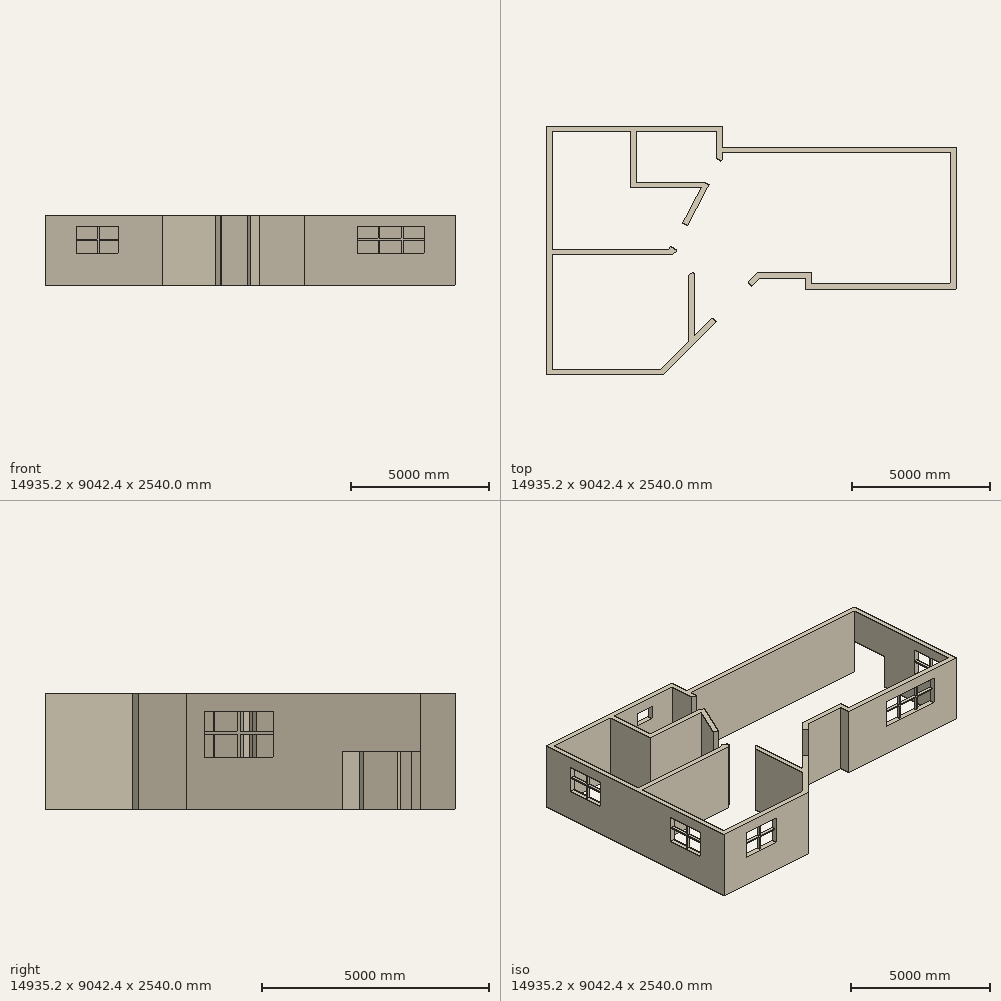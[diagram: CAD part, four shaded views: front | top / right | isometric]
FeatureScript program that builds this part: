
annotation { "Feature Type Name" : "Feature", "Feature Type Description" : "" }
export const myFeature = defineFeature(function(context is Context, id is Id, definition is map)
    precondition{}
    {
        {
            var Q0;
            Q0=qCreatedBy(makeId("Top.planeOp"),FACE);
            var sketch = newSketch(context, id + "F0", { "sketchPlane" : qUnion([Q0])});
            skLineSegment(sketch, "E0.bottom", {"start": v(0, 0) * mm, "end": v(14935.2, 0) * mm});
            skLineSegment(sketch, "E0.top", {"start": v(0, 10668) * mm, "end": v(14935.2, 10668) * mm});
            skLineSegment(sketch, "E0.left", {"start": v(0, 0) * mm, "end": v(0, 10668) * mm});
            skLineSegment(sketch, "E0.right", {"start": v(14935.2, 0) * mm, "end": v(14935.2, 10668) * mm});
            skLineSegment(sketch, "E1", {"start": v(6400.8, 10668) * mm, "end": v(6400.8, 9906) * mm});
            skLineSegment(sketch, "E2", {"start": v(6400.8, 9906) * mm, "end": v(14935.2, 9906) * mm});
            skLineSegment(sketch, "E3", {"start": v(0, 1625.6) * mm, "end": v(4279.65, 1625.6) * mm});
            skLineSegment(sketch, "E4", {"start": v(203.2, 1828.8) * mm, "end": v(2071.3, 1828.8) * mm});
            skLineSegment(sketch, "E5", {"start": v(203.2, 1828.8) * mm, "end": v(203.2, 5994.4) * mm});
            skLineSegment(sketch, "E6", {"start": v(203.2, 10464.8) * mm, "end": v(3073.4, 10464.8) * mm});
            skLineSegment(sketch, "E7", {"start": v(6197.6, 10464.8) * mm, "end": v(6197.6, 9702.8) * mm});
            skLineSegment(sketch, "E8", {"start": v(6400.8, 9702.8) * mm, "end": v(14732, 9702.8) * mm});
            skLineSegment(sketch, "E9", {"start": v(3073.4, 10464.8) * mm, "end": v(3073.4, 8432.8) * mm});
            skLineSegment(sketch, "E10", {"start": v(3073.4, 8432.8) * mm, "end": v(5640.45, 8432.8) * mm});
            skLineSegment(sketch, "E11", {"start": v(3276.6, 8636) * mm, "end": v(5746.81, 8636) * mm});
            skLineSegment(sketch, "E12", {"start": v(3276.6, 8636) * mm, "end": v(3276.6, 10464.8) * mm});
            skLineSegment(sketch, "E13", {"start": v(203.2, 6197.6) * mm, "end": v(4470.4, 6197.6) * mm});
            skLineSegment(sketch, "E14", {"start": v(203.2, 5994.4) * mm, "end": v(4592.55, 5994.4) * mm});
            skLineSegment(sketch, "E15", {"start": v(6400.8, 9702.8) * mm, "end": v(6400.8, 9448.8) * mm});
            skLineSegment(sketch, "E16", {"start": v(6197.6, 9497.16) * mm, "end": v(6197.6, 9702.8) * mm});
            skLineSegment(sketch, "E17", {"start": v(6197.6, 9497.16) * mm, "end": v(6194.44, 9491.13) * mm});
            skLineSegment(sketch, "E18", {"start": v(5143.93, 7047.74) * mm, "end": v(5926.18, 8542.1) * mm});
            skLineSegment(sketch, "E19.trimOffspring", {"start": v(5640.45, 8432.8) * mm, "end": v(4964.57, 7141.63) * mm});
            skLineSegment(sketch, "E20.trimOffspring", {"start": v(203.2, 6197.6) * mm, "end": v(203.2, 10464.8) * mm});
            skLineSegment(sketch, "E21", {"start": v(9448.8, 4724.4) * mm, "end": v(14935.2, 4724.4) * mm});
            skLineSegment(sketch, "E22", {"start": v(9652, 4927.6) * mm, "end": v(14732, 4927.6) * mm});
            skPoint(sketch, "E23.orphan", {"position": v(9448.8, 3711.85) * mm});
            skPoint(sketch, "E24.orphan", {"position": v(14935.2, 3711.85) * mm});
            skLineSegment(sketch, "E25", {"start": v(14732, 9702.8) * mm, "end": v(14732, 4927.6) * mm});
            skPoint(sketch, "E26.trimOffspring.end.orphan", {"position": v(3962.4, 3711.85) * mm});
            skLineSegment(sketch, "E27", {"start": v(9652, 4927.6) * mm, "end": v(9652, 5334) * mm});
            skLineSegment(sketch, "E28", {"start": v(9652, 5334) * mm, "end": v(7700.69, 5334) * mm});
            skLineSegment(sketch, "E29", {"start": v(7784.85, 5130.8) * mm, "end": v(9448.8, 5130.8) * mm});
            skLineSegment(sketch, "E30", {"start": v(9448.8, 5130.8) * mm, "end": v(9448.8, 4724.4) * mm});
            skPoint(sketch, "E31.orphan", {"position": v(9652, 4724.4) * mm});
            skLineSegment(sketch, "E32", {"start": v(2071.3, 1828.8) * mm, "end": v(4195.49, 1828.8) * mm});
            skLineSegment(sketch, "E33", {"start": v(4195.49, 1828.8) * mm, "end": v(5181.9, 2815.22) * mm});
            skLineSegment(sketch, "E34", {"start": v(4279.65, 1625.6) * mm, "end": v(6192, 3537.95) * mm});
            skPoint(sketch, "E35.orphan", {"position": v(4195.49, 1625.6) * mm});
            skLineSegment(sketch, "E36", {"start": v(5181.9, 5230.03) * mm, "end": v(5181.9, 2815.22) * mm});
            skLineSegment(sketch, "E37", {"start": v(4696.3, 6192.61) * mm, "end": v(4753.47, 6118.48) * mm});
            skLineSegment(sketch, "E38", {"start": v(5385.1, 5299.27) * mm, "end": v(5385.1, 3018.42) * mm});
            skLineSegment(sketch, "E39.trimOffspring", {"start": v(5385.1, 3018.42) * mm, "end": v(6048.32, 3681.63) * mm});
            skLineSegment(sketch, "E40", {"start": v(7341.48, 4974.79) * mm, "end": v(7485.16, 4831.1) * mm});
            skLineSegment(sketch, "E41", {"start": v(6048.32, 3681.63) * mm, "end": v(6192, 3537.95) * mm});
            skLineSegment(sketch, "E42.trimOffspring", {"start": v(7485.16, 4831.1) * mm, "end": v(7784.85, 5130.8) * mm});
            skLineSegment(sketch, "E43.trimOffspring", {"start": v(7341.48, 4974.79) * mm, "end": v(7700.69, 5334) * mm});
            skLineSegment(sketch, "E44", {"start": v(4592.55, 5994.4) * mm, "end": v(4753.47, 6118.48) * mm});
            skLineSegment(sketch, "E45", {"start": v(5181.9, 5230.03) * mm, "end": v(5342.83, 5354.1) * mm});
            skLineSegment(sketch, "E46.trimOffspring", {"start": v(5342.83, 5354.1) * mm, "end": v(5385.1, 5299.27) * mm});
            skLineSegment(sketch, "E47", {"start": v(4696.3, 6192.61) * mm, "end": v(4516.94, 6286.5) * mm});
            skLineSegment(sketch, "E48", {"start": v(5143.93, 7047.74) * mm, "end": v(4964.57, 7141.63) * mm});
            skLineSegment(sketch, "E49.trimOffspring", {"start": v(4516.94, 6286.5) * mm, "end": v(4470.4, 6197.6) * mm});
            skLineSegment(sketch, "E50", {"start": v(5746.81, 8636) * mm, "end": v(5926.18, 8542.1) * mm});
            skLineSegment(sketch, "E51", {"start": v(6194.44, 9491.13) * mm, "end": v(6373.8, 9397.23) * mm});
            skLineSegment(sketch, "E52.trimOffspring", {"start": v(6373.8, 9397.23) * mm, "end": v(6400.8, 9448.8) * mm});
            skPoint(sketch, "E53.orphan", {"position": v(3073.4, 10668) * mm});
            skLineSegment(sketch, "E54.trimOffspring", {"start": v(3276.6, 10464.8) * mm, "end": v(6197.6, 10464.8) * mm});
            skPoint(sketch, "E55.orphan", {"position": v(3276.6, 10668) * mm});
            skSolve(sketch);
        }
        {
            var Q0;
            {var subQ14=sQuery(id+"F0.wireOp",EDGE,"E1");Q0=makeQuery(id+"F0.imprint","IMPRINT",FACE,{"disambiguationData":[TD([[makeQuery(id+"F0.imprint","IMPRINT",EDGE,{"derivedFrom":subQ14}),-1.0]])]});}
            extrude(context, id + "F1", {"entities" : qUnion([Q0]), "depth" : 2540 * mm, "offsetDistance" : 25.4 * mm});
        }
        {
            var Q0;
            Q0=makeQuery(id+"F1.opExtrude","SWEPT_FACE",FACE,{"disambiguationData":[OSD([sQuery(id+"F0.wireOp",EDGE,"E0.left")])]});
            var sketch = newSketch(context, id + "F2", { "sketchPlane" : qUnion([Q0])});
            skLineSegment(sketch, "E56.bottom", {"start": v(-9448.8, 2159) * mm, "end": v(-7924.8, 2159) * mm});
            skLineSegment(sketch, "E56.top", {"start": v(-9448.8, 1143) * mm, "end": v(-7924.8, 1143) * mm});
            skLineSegment(sketch, "E56.left", {"start": v(-9448.8, 2159) * mm, "end": v(-9448.8, 1143) * mm});
            skLineSegment(sketch, "E56.right", {"start": v(-7924.8, 2159) * mm, "end": v(-7924.8, 1143) * mm});
            skLineSegment(sketch, "E57.bottom", {"start": v(-4368.8, 2159) * mm, "end": v(-2844.8, 2159) * mm});
            skLineSegment(sketch, "E57.top", {"start": v(-4368.8, 1143) * mm, "end": v(-2844.8, 1143) * mm});
            skLineSegment(sketch, "E57.left", {"start": v(-4368.8, 2159) * mm, "end": v(-4368.8, 1143) * mm});
            skLineSegment(sketch, "E57.right", {"start": v(-2844.8, 2159) * mm, "end": v(-2844.8, 1143) * mm});
            skLineSegment(sketch, "E58.bottom", {"start": v(-8712.2, 2159) * mm, "end": v(-8661.4, 2159) * mm});
            skLineSegment(sketch, "E58.top", {"start": v(-8712.2, 1143) * mm, "end": v(-8661.4, 1143) * mm});
            skLineSegment(sketch, "E58.left", {"start": v(-8712.2, 2159) * mm, "end": v(-8712.2, 1701.8) * mm});
            skLineSegment(sketch, "E58.right", {"start": v(-8661.4, 2159) * mm, "end": v(-8661.4, 1701.8) * mm});
            skLineSegment(sketch, "E59.bottom", {"start": v(-9448.8, 1701.8) * mm, "end": v(-8712.2, 1701.8) * mm});
            skLineSegment(sketch, "E59.top", {"start": v(-9448.8, 1651) * mm, "end": v(-8712.2, 1651) * mm});
            skLineSegment(sketch, "E59.left", {"start": v(-9448.8, 1701.8) * mm, "end": v(-9448.8, 1651) * mm});
            skLineSegment(sketch, "E59.right", {"start": v(-7924.8, 1701.8) * mm, "end": v(-7924.8, 1651) * mm});
            skLineSegment(sketch, "E60.bottom", {"start": v(-4368.8, 1701.8) * mm, "end": v(-3632.2, 1701.8) * mm});
            skLineSegment(sketch, "E60.top", {"start": v(-4368.8, 1651) * mm, "end": v(-3632.2, 1651) * mm});
            skLineSegment(sketch, "E60.left", {"start": v(-4368.8, 1701.8) * mm, "end": v(-4368.8, 1651) * mm});
            skLineSegment(sketch, "E60.right", {"start": v(-2844.8, 1701.8) * mm, "end": v(-2844.8, 1651) * mm});
            skLineSegment(sketch, "E61.bottom", {"start": v(-3632.2, 2159) * mm, "end": v(-3581.4, 2159) * mm});
            skLineSegment(sketch, "E61.top", {"start": v(-3632.2, 1143) * mm, "end": v(-3581.4, 1143) * mm});
            skLineSegment(sketch, "E61.left", {"start": v(-3632.2, 2159) * mm, "end": v(-3632.2, 1701.8) * mm});
            skLineSegment(sketch, "E61.right", {"start": v(-3581.4, 2159) * mm, "end": v(-3581.4, 1701.8) * mm});
            skLineSegment(sketch, "E62.trimOffspring", {"start": v(-8661.4, 1701.8) * mm, "end": v(-7924.8, 1701.8) * mm});
            skLineSegment(sketch, "E63.trimOffspring", {"start": v(-8712.2, 1651) * mm, "end": v(-8712.2, 1143) * mm});
            skLineSegment(sketch, "E64.trimOffspring", {"start": v(-8661.4, 1651) * mm, "end": v(-7924.8, 1651) * mm});
            skLineSegment(sketch, "E65.trimOffspring", {"start": v(-8661.4, 1651) * mm, "end": v(-8661.4, 1143) * mm});
            skLineSegment(sketch, "E66.trimOffspring", {"start": v(-3581.4, 1701.8) * mm, "end": v(-2844.8, 1701.8) * mm});
            skLineSegment(sketch, "E67.trimOffspring", {"start": v(-3632.2, 1651) * mm, "end": v(-3632.2, 1143) * mm});
            skLineSegment(sketch, "E68.trimOffspring", {"start": v(-3581.4, 1651) * mm, "end": v(-2844.8, 1651) * mm});
            skLineSegment(sketch, "E69.trimOffspring", {"start": v(-3581.4, 1651) * mm, "end": v(-3581.4, 1143) * mm});
            skSolve(sketch);
        }
        {
            var Q0;
            {var subQ0=sQuery(id+"F2.wireOp",EDGE,"E58.left");Q0=makeQuery(id+"F2.imprint","IMPRINT",FACE,{"disambiguationData":[TD([[makeQuery(id+"F2.imprint","IMPRINT",EDGE,{"derivedFrom":subQ0}),-1.0]])]});}
            var Q1;
            {var subQ0=sQuery(id+"F2.wireOp",EDGE,"E58.right");Q1=makeQuery(id+"F2.imprint","IMPRINT",FACE,{"disambiguationData":[TD([[makeQuery(id+"F2.imprint","IMPRINT",EDGE,{"derivedFrom":subQ0}),1.0]])]});}
            var Q2;
            {var subQ4=sQuery(id+"F2.wireOp",EDGE,"E59.top");Q2=makeQuery(id+"F2.imprint","IMPRINT",FACE,{"disambiguationData":[TD([[makeQuery(id+"F2.imprint","IMPRINT",EDGE,{"derivedFrom":subQ4}),-1.0]])]});}
            var Q3;
            {var subQ4=sQuery(id+"F2.wireOp",EDGE,"E64.trimOffspring");Q3=makeQuery(id+"F2.imprint","IMPRINT",FACE,{"disambiguationData":[TD([[makeQuery(id+"F2.imprint","IMPRINT",EDGE,{"derivedFrom":subQ4}),-1.0]])]});}
            var Q4;
            {var subQ4=sQuery(id+"F2.wireOp",EDGE,"E60.bottom");Q4=makeQuery(id+"F2.imprint","IMPRINT",FACE,{"disambiguationData":[TD([[makeQuery(id+"F2.imprint","IMPRINT",EDGE,{"derivedFrom":subQ4}),1.0]])]});}
            var Q5;
            {var subQ0=sQuery(id+"F2.wireOp",EDGE,"E61.right");Q5=makeQuery(id+"F2.imprint","IMPRINT",FACE,{"disambiguationData":[TD([[makeQuery(id+"F2.imprint","IMPRINT",EDGE,{"derivedFrom":subQ0}),1.0]])]});}
            var Q6;
            {var subQ4=sQuery(id+"F2.wireOp",EDGE,"E60.top");Q6=makeQuery(id+"F2.imprint","IMPRINT",FACE,{"disambiguationData":[TD([[makeQuery(id+"F2.imprint","IMPRINT",EDGE,{"derivedFrom":subQ4}),-1.0]])]});}
            var Q7;
            {var subQ4=sQuery(id+"F2.wireOp",EDGE,"E68.trimOffspring");Q7=makeQuery(id+"F2.imprint","IMPRINT",FACE,{"disambiguationData":[TD([[makeQuery(id+"F2.imprint","IMPRINT",EDGE,{"derivedFrom":subQ4}),-1.0]])]});}
            extrude(context, id + "F3", {"entities" : qUnion([Q0, Q1, Q2, Q3, Q4, Q5, Q6, Q7]), "operationType" : NewBodyOperationType.REMOVE, "oppositeDirection" : true, "depth" : 203.2 * mm, "offsetDistance" : 25.4 * mm});
        }
        {
            var Q0;
            Q0=makeQuery(id+"F1.opExtrude","SWEPT_FACE",FACE,{"disambiguationData":[OSD([sQuery(id+"F0.wireOp",EDGE,"E0.left")])]});
            var sketch = newSketch(context, id + "F4", { "sketchPlane" : qUnion([Q0])});
            skLineSegment(sketch, "E70.bottom", {"start": v(-9448.8, 2159) * mm, "end": v(-7924.8, 2159) * mm});
            skLineSegment(sketch, "E70.top", {"start": v(-9448.8, 1143) * mm, "end": v(-7924.8, 1143) * mm});
            skLineSegment(sketch, "E70.left", {"start": v(-9448.8, 2159) * mm, "end": v(-9448.8, 1143) * mm});
            skLineSegment(sketch, "E70.right", {"start": v(-7924.8, 2159) * mm, "end": v(-7924.8, 1143) * mm});
            skLineSegment(sketch, "E71.bottom", {"start": v(-4368.8, 2159) * mm, "end": v(-2844.8, 2159) * mm});
            skLineSegment(sketch, "E71.top", {"start": v(-4368.8, 1143) * mm, "end": v(-2844.8, 1143) * mm});
            skLineSegment(sketch, "E71.left", {"start": v(-4368.8, 2159) * mm, "end": v(-4368.8, 1143) * mm});
            skLineSegment(sketch, "E71.right", {"start": v(-2844.8, 2159) * mm, "end": v(-2844.8, 1143) * mm});
            skSolve(sketch);
        }
        {
            var Q0;
            Q0 = qSketchRegion(id + "F4", true);
            extrude(context, id + "F5", {"entities" : qUnion([Q0]), "operationType" : NewBodyOperationType.REMOVE, "oppositeDirection" : true, "depth" : 76.2 * mm, "offsetDistance" : 25.4 * mm});
        }
        {
            var Q0;
            Q0=makeQuery(id+"F1.opExtrude","SWEPT_FACE",FACE,{"disambiguationData":[OSD([sQuery(id+"F0.wireOp",EDGE,"E3")])]});
            var sketch = newSketch(context, id + "F6", { "sketchPlane" : qUnion([Q0])});
            skLineSegment(sketch, "E72.bottom", {"start": v(1143, 2159) * mm, "end": v(2667, 2159) * mm});
            skLineSegment(sketch, "E72.top", {"start": v(1143, 1143) * mm, "end": v(2667, 1143) * mm});
            skLineSegment(sketch, "E72.left", {"start": v(1143, 2159) * mm, "end": v(1143, 1143) * mm});
            skLineSegment(sketch, "E72.right", {"start": v(2667, 2159) * mm, "end": v(2667, 1143) * mm});
            skLineSegment(sketch, "E73.bottom", {"start": v(1905, 2159) * mm, "end": v(1955.8, 2159) * mm});
            skLineSegment(sketch, "E73.top", {"start": v(1905, 1143) * mm, "end": v(1955.8, 1143) * mm});
            skLineSegment(sketch, "E73.left", {"start": v(1905, 2159) * mm, "end": v(1905, 1676.4) * mm});
            skLineSegment(sketch, "E73.right", {"start": v(1955.8, 2159) * mm, "end": v(1955.8, 1676.4) * mm});
            skLineSegment(sketch, "E74.bottom", {"start": v(1143, 1676.4) * mm, "end": v(1905, 1676.4) * mm});
            skLineSegment(sketch, "E74.top", {"start": v(1143, 1625.6) * mm, "end": v(1905, 1625.6) * mm});
            skLineSegment(sketch, "E74.left", {"start": v(1143, 1676.4) * mm, "end": v(1143, 1625.6) * mm});
            skLineSegment(sketch, "E74.right", {"start": v(2667, 1676.4) * mm, "end": v(2667, 1625.6) * mm});
            skLineSegment(sketch, "E75.trimOffspring", {"start": v(1955.8, 1676.4) * mm, "end": v(2667, 1676.4) * mm});
            skLineSegment(sketch, "E76.trimOffspring", {"start": v(1955.8, 1625.6) * mm, "end": v(1955.8, 1143) * mm});
            skLineSegment(sketch, "E77.trimOffspring", {"start": v(1955.8, 1625.6) * mm, "end": v(2667, 1625.6) * mm});
            skLineSegment(sketch, "E78.trimOffspring", {"start": v(1905, 1625.6) * mm, "end": v(1905, 1143) * mm});
            skSolve(sketch);
        }
        {
            var Q0;
            {var subQ3=sQuery(id+"F6.wireOp",EDGE,"E73.left");Q0=makeQuery(id+"F6.imprint","IMPRINT",FACE,{"disambiguationData":[TD([[makeQuery(id+"F6.imprint","IMPRINT",EDGE,{"derivedFrom":subQ3}),-1.0]])]});}
            var Q1;
            {var subQ0=sQuery(id+"F6.wireOp",EDGE,"E73.right");Q1=makeQuery(id+"F6.imprint","IMPRINT",FACE,{"disambiguationData":[TD([[makeQuery(id+"F6.imprint","IMPRINT",EDGE,{"derivedFrom":subQ0}),1.0]])]});}
            var Q2;
            {var subQ4=sQuery(id+"F6.wireOp",EDGE,"E74.top");Q2=makeQuery(id+"F6.imprint","IMPRINT",FACE,{"disambiguationData":[TD([[makeQuery(id+"F6.imprint","IMPRINT",EDGE,{"derivedFrom":subQ4}),-1.0]])]});}
            var Q3;
            {var subQ0=sQuery(id+"F6.wireOp",EDGE,"E76.trimOffspring");Q3=makeQuery(id+"F6.imprint","IMPRINT",FACE,{"disambiguationData":[TD([[makeQuery(id+"F6.imprint","IMPRINT",EDGE,{"derivedFrom":subQ0}),1.0]])]});}
            extrude(context, id + "F7", {"entities" : qUnion([Q0, Q1, Q2, Q3]), "operationType" : NewBodyOperationType.REMOVE, "oppositeDirection" : true, "depth" : 203.2 * mm, "offsetDistance" : 25.4 * mm});
        }
        {
            var Q0;
            Q0=makeQuery(id+"F1.opExtrude","SWEPT_FACE",FACE,{"disambiguationData":[OSD([sQuery(id+"F0.wireOp",EDGE,"E3")])]});
            var sketch = newSketch(context, id + "F8", { "sketchPlane" : qUnion([Q0])});
            skLineSegment(sketch, "E79.bottom", {"start": v(1143, 2159) * mm, "end": v(2667, 2159) * mm});
            skLineSegment(sketch, "E79.top", {"start": v(1143, 1143) * mm, "end": v(2667, 1143) * mm});
            skLineSegment(sketch, "E79.left", {"start": v(1143, 2159) * mm, "end": v(1143, 1143) * mm});
            skLineSegment(sketch, "E79.right", {"start": v(2667, 2159) * mm, "end": v(2667, 1143) * mm});
            skSolve(sketch);
        }
        {
            var Q0;
            Q0 = qSketchRegion(id + "F8", true);
            extrude(context, id + "F9", {"entities" : qUnion([Q0]), "operationType" : NewBodyOperationType.REMOVE, "oppositeDirection" : true, "depth" : 76.2 * mm, "offsetDistance" : 25.4 * mm});
        }
        {
            var Q0;
            Q0=makeQuery(id+"F1.opExtrude","SWEPT_FACE",FACE,{"disambiguationData":[OSD([sQuery(id+"F0.wireOp",EDGE,"E21")])]});
            var sketch = newSketch(context, id + "F10", { "sketchPlane" : qUnion([Q0])});
            skLineSegment(sketch, "E80.bottom", {"start": v(11353.8, 2159) * mm, "end": v(13792.2, 2159) * mm});
            skLineSegment(sketch, "E80.top", {"start": v(11353.8, 1143) * mm, "end": v(13792.2, 1143) * mm});
            skLineSegment(sketch, "E80.left", {"start": v(11353.8, 2159) * mm, "end": v(11353.8, 1143) * mm});
            skLineSegment(sketch, "E80.right", {"start": v(13792.2, 2159) * mm, "end": v(13792.2, 1143) * mm});
            skLineSegment(sketch, "E81.bottom", {"start": v(11353.8, 1701.8) * mm, "end": v(12115.8, 1701.8) * mm});
            skLineSegment(sketch, "E81.top", {"start": v(11353.8, 1651) * mm, "end": v(12115.8, 1651) * mm});
            skLineSegment(sketch, "E81.left", {"start": v(11353.8, 1701.8) * mm, "end": v(11353.8, 1651) * mm});
            skLineSegment(sketch, "E81.right", {"start": v(13792.2, 1701.8) * mm, "end": v(13792.2, 1651) * mm});
            skLineSegment(sketch, "E82.top", {"start": v(12115.8, 1143) * mm, "end": v(12166.6, 1143) * mm});
            skLineSegment(sketch, "E82.left", {"start": v(12115.8, 2159) * mm, "end": v(12115.8, 1701.8) * mm});
            skLineSegment(sketch, "E82.right", {"start": v(12166.6, 2159) * mm, "end": v(12166.6, 1701.8) * mm});
            skLineSegment(sketch, "E83.top", {"start": v(12979.4, 1143) * mm, "end": v(13030.2, 1143) * mm});
            skLineSegment(sketch, "E83.left", {"start": v(12979.4, 2159) * mm, "end": v(12979.4, 1701.8) * mm});
            skLineSegment(sketch, "E83.right", {"start": v(13030.2, 2159) * mm, "end": v(13030.2, 1701.8) * mm});
            skPoint(sketch, "E82.bottom.start.orphan", {"position": v(12115.8, 2320.15) * mm});
            skLineSegment(sketch, "E84.trimOffspring", {"start": v(13030.2, 1651) * mm, "end": v(13792.2, 1651) * mm});
            skLineSegment(sketch, "E85.trimOffspring", {"start": v(13030.2, 1651) * mm, "end": v(13030.2, 1143) * mm});
            skLineSegment(sketch, "E86.trimOffspring", {"start": v(13030.2, 1701.8) * mm, "end": v(13792.2, 1701.8) * mm});
            skLineSegment(sketch, "E87.trimOffspring", {"start": v(12979.4, 1651) * mm, "end": v(12979.4, 1143) * mm});
            skLineSegment(sketch, "E88.trimOffspring", {"start": v(12166.6, 1701.8) * mm, "end": v(12979.4, 1701.8) * mm});
            skLineSegment(sketch, "E89.trimOffspring", {"start": v(12115.8, 1651) * mm, "end": v(12115.8, 1143) * mm});
            skLineSegment(sketch, "E90.trimOffspring", {"start": v(12166.6, 1651) * mm, "end": v(12979.4, 1651) * mm});
            skLineSegment(sketch, "E91.trimOffspring", {"start": v(12166.6, 1651) * mm, "end": v(12166.6, 1143) * mm});
            skSolve(sketch);
        }
        {
            var Q0;
            {var subQ4=sQuery(id+"F10.wireOp",EDGE,"E81.bottom");Q0=makeQuery(id+"F10.imprint","IMPRINT",FACE,{"disambiguationData":[TD([[makeQuery(id+"F10.imprint","IMPRINT",EDGE,{"derivedFrom":subQ4}),1.0]])]});}
            var Q1;
            {var subQ0=sQuery(id+"F10.wireOp",EDGE,"E82.right");Q1=makeQuery(id+"F10.imprint","IMPRINT",FACE,{"disambiguationData":[TD([[makeQuery(id+"F10.imprint","IMPRINT",EDGE,{"derivedFrom":subQ0}),1.0]])]});}
            var Q2;
            {var subQ0=sQuery(id+"F10.wireOp",EDGE,"E83.right");Q2=makeQuery(id+"F10.imprint","IMPRINT",FACE,{"disambiguationData":[TD([[makeQuery(id+"F10.imprint","IMPRINT",EDGE,{"derivedFrom":subQ0}),1.0]])]});}
            var Q3;
            {var subQ4=sQuery(id+"F10.wireOp",EDGE,"E81.top");Q3=makeQuery(id+"F10.imprint","IMPRINT",FACE,{"disambiguationData":[TD([[makeQuery(id+"F10.imprint","IMPRINT",EDGE,{"derivedFrom":subQ4}),-1.0]])]});}
            var Q4;
            {var subQ2=sQuery(id+"F10.wireOp",EDGE,"E87.trimOffspring");Q4=makeQuery(id+"F10.imprint","IMPRINT",FACE,{"disambiguationData":[TD([[makeQuery(id+"F10.imprint","IMPRINT",EDGE,{"derivedFrom":subQ2}),-1.0]])]});}
            var Q5;
            {var subQ4=sQuery(id+"F10.wireOp",EDGE,"E84.trimOffspring");Q5=makeQuery(id+"F10.imprint","IMPRINT",FACE,{"disambiguationData":[TD([[makeQuery(id+"F10.imprint","IMPRINT",EDGE,{"derivedFrom":subQ4}),-1.0]])]});}
            extrude(context, id + "F11", {"entities" : qUnion([Q0, Q1, Q2, Q3, Q4, Q5]), "operationType" : NewBodyOperationType.REMOVE, "oppositeDirection" : true, "depth" : 203.2 * mm, "offsetDistance" : 25.4 * mm});
        }
        {
            var Q0;
            Q0=makeQuery(id+"F1.opExtrude","SWEPT_FACE",FACE,{"disambiguationData":[OSD([sQuery(id+"F0.wireOp",EDGE,"E21")])]});
            var sketch = newSketch(context, id + "F12", { "sketchPlane" : qUnion([Q0])});
            skLineSegment(sketch, "E92.bottom", {"start": v(11353.8, 2159) * mm, "end": v(13792.2, 2159) * mm});
            skLineSegment(sketch, "E92.top", {"start": v(11353.8, 1143) * mm, "end": v(13792.2, 1143) * mm});
            skLineSegment(sketch, "E92.left", {"start": v(11353.8, 2159) * mm, "end": v(11353.8, 1143) * mm});
            skLineSegment(sketch, "E92.right", {"start": v(13792.2, 2159) * mm, "end": v(13792.2, 1143) * mm});
            skSolve(sketch);
        }
        {
            var Q0;
            Q0 = qSketchRegion(id + "F12", true);
            extrude(context, id + "F13", {"entities" : qUnion([Q0]), "operationType" : NewBodyOperationType.REMOVE, "oppositeDirection" : true, "depth" : 76.2 * mm, "offsetDistance" : 25.4 * mm});
        }
        {
            var Q0;
            Q0=makeQuery(id+"F1.opExtrude","SWEPT_FACE",FACE,{"disambiguationData":[OSD([sQuery(id+"F0.wireOp",EDGE,"E0.top")])]});
            var sketch = newSketch(context, id + "F14", { "sketchPlane" : qUnion([Q0])});
            skLineSegment(sketch, "E93.bottom", {"start": v(-5181.6, 2159) * mm, "end": v(-4419.6, 2159) * mm});
            skLineSegment(sketch, "E93.top", {"start": v(-5181.6, 1651) * mm, "end": v(-4419.6, 1651) * mm});
            skLineSegment(sketch, "E93.left", {"start": v(-5181.6, 2159) * mm, "end": v(-5181.6, 1651) * mm});
            skLineSegment(sketch, "E93.right", {"start": v(-4419.6, 2159) * mm, "end": v(-4419.6, 1651) * mm});
            skSolve(sketch);
        }
        {
            var Q0;
            Q0=makeQuery(id+"F14.imprint","IMPRINT",FACE,{"disambiguationData":[TD([[makeQuery(id+"F14.imprint","IMPRINT",EDGE,{"derivedFrom":sQuery(id+"F14.wireOp",EDGE,"E93.bottom")}),-1.0]])]});
            extrude(context, id + "F15", {"entities" : qUnion([Q0]), "operationType" : NewBodyOperationType.REMOVE, "oppositeDirection" : true, "depth" : 203.2 * mm, "offsetDistance" : 25.4 * mm});
        }
        {
            var Q0;
            Q0=makeQuery(id+"F1.opExtrude","SWEPT_FACE",FACE,{"disambiguationData":[OSD([sQuery(id+"F0.wireOp",EDGE,"E0.right")])]});
            var sketch = newSketch(context, id + "F16", { "sketchPlane" : qUnion([Q0])});
            skLineSegment(sketch, "E94.bottom", {"start": v(9906, 1270) * mm, "end": v(8178.8, 1270) * mm});
            skLineSegment(sketch, "E94.top", {"start": v(9906, 0) * mm, "end": v(8178.8, 0) * mm});
            skLineSegment(sketch, "E94.left", {"start": v(9906, 1270) * mm, "end": v(9906, 0) * mm});
            skLineSegment(sketch, "E94.right", {"start": v(8178.8, 1270) * mm, "end": v(8178.8, 0) * mm});
            skLineSegment(sketch, "E95", {"start": v(9702.8, 1270) * mm, "end": v(9702.8, 0) * mm});
            skSolve(sketch);
        }
        {
            var Q0;
            Q0 = qSketchRegion(id + "F16", true);
            extrude(context, id + "F17", {"entities" : qUnion([Q0]), "operationType" : NewBodyOperationType.REMOVE, "oppositeDirection" : true, "depth" : 203.2 * mm, "offsetDistance" : 25.4 * mm});
        }
        {
            var Q0;
            Q0=makeQuery(id+"F1.opExtrude","SWEPT_FACE",FACE,{"disambiguationData":[OSD([sQuery(id+"F0.wireOp",EDGE,"E0.right")])]});
            var sketch = newSketch(context, id + "F18", { "sketchPlane" : qUnion([Q0])});
            skLineSegment(sketch, "E96.bottom", {"start": v(5130.8, 2159) * mm, "end": v(6654.8, 2159) * mm});
            skLineSegment(sketch, "E96.top", {"start": v(5130.8, 1143) * mm, "end": v(6654.8, 1143) * mm});
            skLineSegment(sketch, "E96.left", {"start": v(5130.8, 2159) * mm, "end": v(5130.8, 1143) * mm});
            skLineSegment(sketch, "E96.right", {"start": v(6654.8, 2159) * mm, "end": v(6654.8, 1143) * mm});
            skLineSegment(sketch, "E97.bottom", {"start": v(5130.8, 1701.8) * mm, "end": v(5867.4, 1701.8) * mm});
            skLineSegment(sketch, "E97.top", {"start": v(5130.8, 1651) * mm, "end": v(5867.4, 1651) * mm});
            skLineSegment(sketch, "E97.left", {"start": v(5130.8, 1701.8) * mm, "end": v(5130.8, 1651) * mm});
            skLineSegment(sketch, "E97.right", {"start": v(6654.8, 1701.8) * mm, "end": v(6654.8, 1651) * mm});
            skLineSegment(sketch, "E98.bottom", {"start": v(5867.4, 2155.34) * mm, "end": v(5918.2, 2155.34) * mm});
            skLineSegment(sketch, "E98.top", {"start": v(5867.4, 1143) * mm, "end": v(5918.2, 1143) * mm});
            skLineSegment(sketch, "E98.left", {"start": v(5867.4, 2155.34) * mm, "end": v(5867.4, 1701.8) * mm});
            skLineSegment(sketch, "E98.right", {"start": v(5918.2, 2155.34) * mm, "end": v(5918.2, 1701.8) * mm});
            skLineSegment(sketch, "E99.trimOffspring", {"start": v(5918.2, 1651) * mm, "end": v(6654.8, 1651) * mm});
            skLineSegment(sketch, "E100.trimOffspring", {"start": v(5918.2, 1651) * mm, "end": v(5918.2, 1143) * mm});
            skLineSegment(sketch, "E101.trimOffspring", {"start": v(5867.4, 1651) * mm, "end": v(5867.4, 1143) * mm});
            skLineSegment(sketch, "E102.trimOffspring", {"start": v(5918.2, 1701.8) * mm, "end": v(6654.8, 1701.8) * mm});
            skSolve(sketch);
        }
        {
            var Q0;
            {var subQ1=sQuery(id+"F18.wireOp",EDGE,"E96.bottom");Q0=makeQuery(id+"F18.imprint","IMPRINT",FACE,{"disambiguationData":[TD([[makeQuery(id+"F18.imprint","IMPRINT",EDGE,{"derivedFrom":subQ1}),-1.0]])]});}
            var Q1;
            {var subQ4=sQuery(id+"F18.wireOp",EDGE,"E97.top");Q1=makeQuery(id+"F18.imprint","IMPRINT",FACE,{"disambiguationData":[TD([[makeQuery(id+"F18.imprint","IMPRINT",EDGE,{"derivedFrom":subQ4}),-1.0]])]});}
            var Q2;
            {var subQ4=sQuery(id+"F18.wireOp",EDGE,"E99.trimOffspring");Q2=makeQuery(id+"F18.imprint","IMPRINT",FACE,{"disambiguationData":[TD([[makeQuery(id+"F18.imprint","IMPRINT",EDGE,{"derivedFrom":subQ4}),-1.0]])]});}
            extrude(context, id + "F19", {"entities" : qUnion([Q0, Q1, Q2]), "operationType" : NewBodyOperationType.REMOVE, "oppositeDirection" : true, "depth" : 203.2 * mm, "offsetDistance" : 25.4 * mm});
        }
        {
            var Q0;
            Q0=makeQuery(id+"F1.opExtrude","SWEPT_FACE",FACE,{"disambiguationData":[OSD([sQuery(id+"F0.wireOp",EDGE,"E0.right")])]});
            var sketch = newSketch(context, id + "F20", { "sketchPlane" : qUnion([Q0])});
            skLineSegment(sketch, "E103.bottom", {"start": v(5130.8, 2159) * mm, "end": v(6654.8, 2159) * mm});
            skLineSegment(sketch, "E103.top", {"start": v(5130.8, 1143) * mm, "end": v(6654.8, 1143) * mm});
            skLineSegment(sketch, "E103.left", {"start": v(5130.8, 2159) * mm, "end": v(5130.8, 1143) * mm});
            skLineSegment(sketch, "E103.right", {"start": v(6654.8, 2159) * mm, "end": v(6654.8, 1143) * mm});
            skSolve(sketch);
        }
        {
            var Q0;
            Q0 = qSketchRegion(id + "F20", true);
            extrude(context, id + "F21", {"entities" : qUnion([Q0]), "operationType" : NewBodyOperationType.REMOVE, "oppositeDirection" : true, "depth" : 76.2 * mm, "offsetDistance" : 25.4 * mm});
        }
    });
